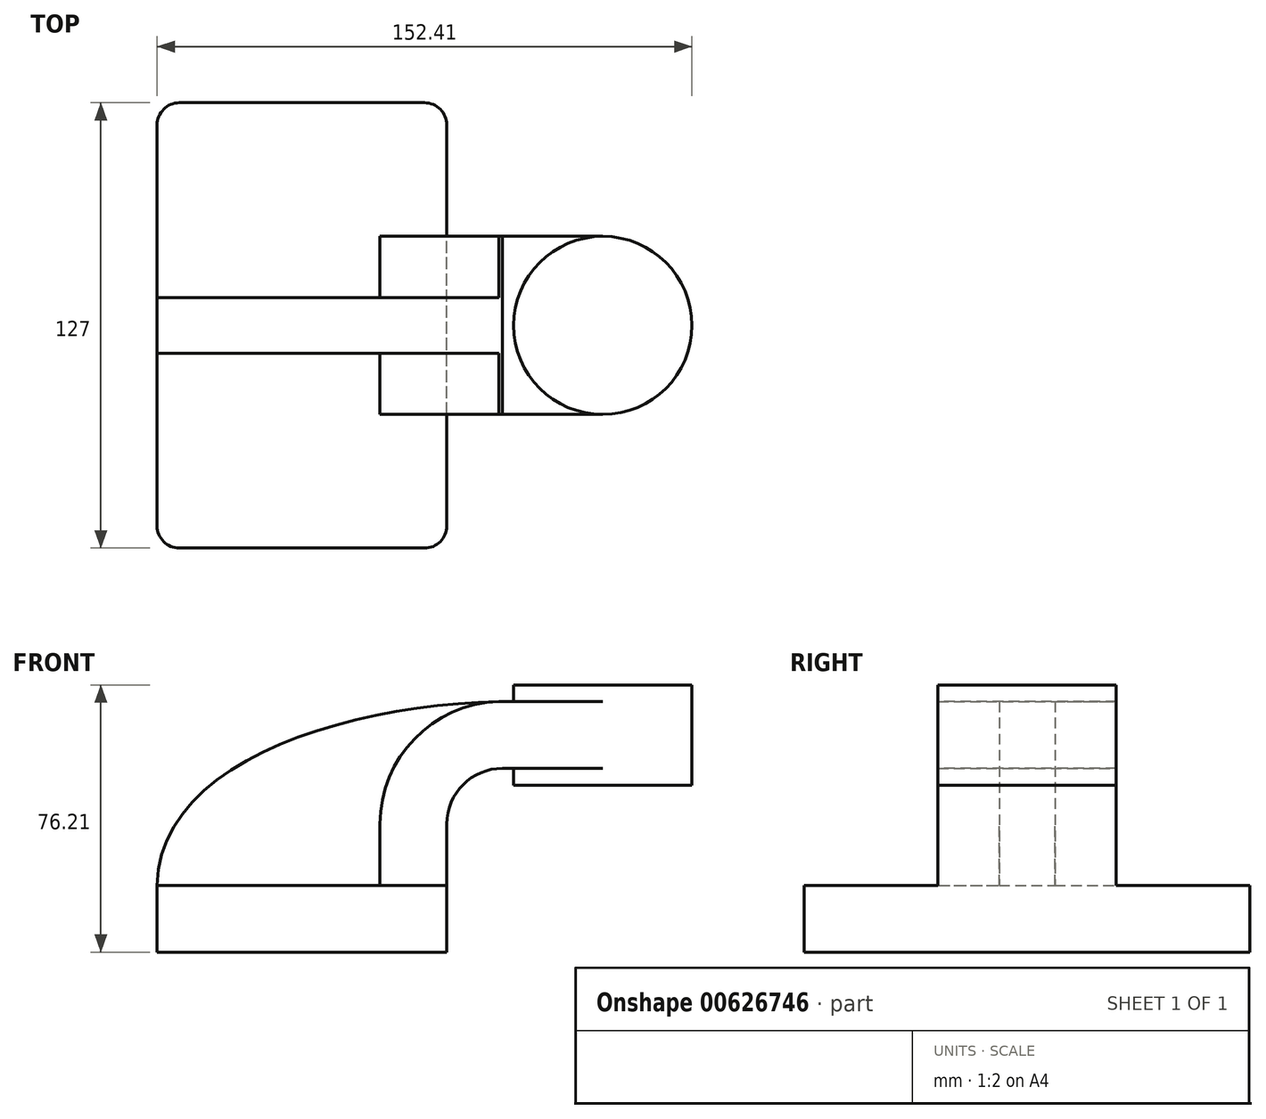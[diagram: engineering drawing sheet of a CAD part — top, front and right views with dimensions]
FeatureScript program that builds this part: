
annotation { "Feature Type Name" : "Feature", "Feature Type Description" : "" }
export const myFeature = defineFeature(function(context is Context, id is Id, definition is map)
    precondition{}
    {
        {
            var Q0;
            Q0=qCreatedBy(makeId("Front.planeOp"),FACE);
            var sketch = newSketch(context, id + "F0", { "sketchPlane" : qUnion([Q0])});
            skLineSegment(sketch, "E0.bottom", {"start": v(41.28, -9.52) * mm, "end": v(-41.27, -9.53) * mm});
            skLineSegment(sketch, "E0.top", {"start": v(41.27, 9.53) * mm, "end": v(-41.28, 9.52) * mm});
            skLineSegment(sketch, "E0.left", {"start": v(41.28, -9.53) * mm, "end": v(41.27, 9.53) * mm});
            skLineSegment(sketch, "E0.right", {"start": v(-41.27, -9.53) * mm, "end": v(-41.28, 9.52) * mm});
            skPoint(sketch, "E0.middle", {"position": v(0, 0) * mm});
            skLineSegment(sketch, "E1.bottom", {"start": v(111.12, 38.1) * mm, "end": v(60.32, 38.1) * mm});
            skLineSegment(sketch, "E1.top", {"start": v(111.12, 66.68) * mm, "end": v(60.32, 66.68) * mm});
            skLineSegment(sketch, "E1.left", {"start": v(111.12, 38.1) * mm, "end": v(111.12, 66.67) * mm});
            skLineSegment(sketch, "E1.right", {"start": v(60.32, 38.1) * mm, "end": v(60.32, 66.67) * mm});
            skPoint(sketch, "E1.middle", {"position": v(85.72, 52.39) * mm});
            skLineSegment(sketch, "E2", {"start": v(41.27, 9.52) * mm, "end": v(41.27, 27) * mm});
            skLineSegment(sketch, "E3", {"start": v(41.27, 27) * mm, "end": v(41.27, 27) * mm});
            skArc(sketch, "E4", {"start": v(41.27, 27) * mm, "mid": v(45.92, 38.23) * mm, "end": v(57.15, 42.88) * mm});
            skLineSegment(sketch, "E5", {"start": v(57.15, 42.88) * mm, "end": v(85.72, 42.88) * mm});
            skLineSegment(sketch, "E6.0", {"start": v(57.15, 61.93) * mm, "end": v(85.72, 61.93) * mm});
            skArc(sketch, "E6.1", {"start": v(22.22, 27) * mm, "mid": v(32.45, 51.7) * mm, "end": v(57.15, 61.93) * mm});
            skLineSegment(sketch, "E6.2", {"start": v(22.22, 9.52) * mm, "end": v(22.22, 27) * mm});
            skLineSegment(sketch, "E7", {"start": v(85.72, 66.68) * mm, "end": v(85.72, 38.1) * mm});
            skFitSpline(sketch, "E8", {"points": [v(57.15, 61.93) * mm, v(-41.28, 9.52) * mm], "startDerivative": vector(-131.4, -1.7) * mm, "endDerivative": vector(-1.6, -106.28) * mm});
            skSolve(sketch);
        }
        {
            var Q0;
            Q0=makeQuery(id+"F0.imprint","IMPRINT",FACE,{"disambiguationData":[TD([[makeQuery(id+"F0.imprint","IMPRINT",EDGE,{"derivedFrom":sQuery(id+"F0.wireOp",EDGE,"E0.bottom")}),-1.0]])]});
            extrude(context, id + "F1", {"entities" : qUnion([Q0]), "endBound" : BoundingType.SYMMETRIC, "depth" : 127 * mm, "offsetDistance" : 25.4 * mm});
        }
        {
            var Q0;
            {var subQ1=sQuery(id+"F0.wireOp",EDGE,"E2");Q0=makeQuery(id+"F0.imprint","IMPRINT",FACE,{"disambiguationData":[TD([[makeQuery(id+"F0.imprint","IMPRINT",EDGE,{"derivedFrom":subQ1}),1.0]])]});}
            var Q1;
            {var subQ0=sQuery(id+"F0.wireOp",EDGE,"E5");var subQ1=sQuery(id+"F0.wireOp",EDGE,"E1.right");var subQ2=makeQuery(id+"F0.imprint","INTERSECT",VERTEX,{"derivedFrom":[subQ1,subQ0]});Q1=makeQuery(id+"F0.imprint","IMPRINT",FACE,{"disambiguationData":[TD([[makeQuery(id+"F0.imprint","IMPRINT",EDGE,{"disambiguationData":[TD([[subQ2,-1.0]])],"derivedFrom":subQ1}),-1.0]])]});}
            extrude(context, id + "F2", {"entities" : qUnion([Q0, Q1]), "operationType" : NewBodyOperationType.ADD, "endBound" : BoundingType.SYMMETRIC, "depth" : 50.8 * mm, "offsetDistance" : 25.4 * mm});
        }
        {
            var Q0;
            {var subQ3=sQuery(id+"F0.wireOp",EDGE,"E6.2");Q0=makeQuery(id+"F0.imprint","IMPRINT",FACE,{"disambiguationData":[TD([[makeQuery(id+"F0.imprint","IMPRINT",EDGE,{"derivedFrom":subQ3}),1.0]])]});}
            extrude(context, id + "F3", {"entities" : qUnion([Q0]), "operationType" : NewBodyOperationType.ADD, "endBound" : BoundingType.SYMMETRIC, "depth" : 15.88 * mm, "offsetDistance" : 25.4 * mm});
        }
        {
            var Q0;
            {var subQ0=sQuery(id+"F0.wireOp",EDGE,"E1.left");Q0=makeQuery(id+"F0.imprint","IMPRINT",FACE,{"disambiguationData":[TD([[makeQuery(id+"F0.imprint","IMPRINT",EDGE,{"derivedFrom":subQ0}),1.0]])]});}
            var Q1;
            Q1=sQuery(id+"F0.wireOp",EDGE,"E7");
            revolve(context, id + "F4", {"operationType" : NewBodyOperationType.ADD, "entities" : qUnion([Q0]), "axis" : qUnion([Q1]), "revolveType" : RevolveType.FULL});
        }
        {
            var Q0;
            Q0=makeQuery(id+"F1.opExtrude","CAP_EDGE",EDGE,{"disambiguationData":[OSD([sQuery(id+"F0.wireOp",EDGE,"E0.left")])],"isStart":false});
            var Q1;
            Q1=makeQuery(id+"F1.opExtrude","CAP_EDGE",EDGE,{"disambiguationData":[OSD([sQuery(id+"F0.wireOp",EDGE,"E0.right")])],"isStart":false});
            var Q2;
            Q2=makeQuery(id+"F1.opExtrude","CAP_EDGE",EDGE,{"disambiguationData":[OSD([sQuery(id+"F0.wireOp",EDGE,"E0.left")])],"isStart":true});
            var Q3;
            Q3=makeQuery(id+"F1.opExtrude","CAP_EDGE",EDGE,{"disambiguationData":[OSD([sQuery(id+"F0.wireOp",EDGE,"E0.right")])],"isStart":true});
            fillet(context, id + "F5", {"entities" : qUnion([Q0, Q1, Q2, Q3]), "radius" : 6.35 * mm, "tangentPropagation" : true, "allowEdgeOverflow" : false});
        }
    });
